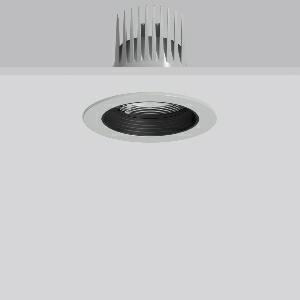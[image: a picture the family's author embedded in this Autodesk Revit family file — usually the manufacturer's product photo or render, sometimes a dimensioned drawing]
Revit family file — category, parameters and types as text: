
# Revit family: heledon_maxi_e_901782_004_777c
name_source: partatom
category: Lighting Fixtures
units: mm (PartAtom-declared; Revit-internal decimal feet)

## family parameters
Cut with Voids When Loaded = No
Host = Face
Light Source = No
Part Type = Normal
Room Calculation Point = No
Round Connector Dimension = Use Diameter
Shared = No

## types (1)
- HELEDON maxi E (1 x LED Modul 920 meat+, 1850 lm, 2000)
    Apparent Load = 33 VA
    Approval mark = CE
    CIE Flux Codes = 96 99 100 100 100
    Color Rendering = 90
    Color Temperature = 2000
    Default Elevation = 1800 mm
    Description = Series: HELEDON maxi
Round recessed downlight. Housing: die-cast aluminium, powder-coated. Black plastic ring and recessed LED to prevent glare from the side. Optical assembly with lens made of plastic (polycarbonate) for the best homogeneous light distribution - can be changed without tools. Special LED for illumination of meat included. Suitable for Recessed ceiling mounting. Installation without tools thanks to spring fastening system. Including separate LED converter with connecting cable 600 mm.High quality converter without flickering and stroboscopic effect. Through-wiring box (5 pole) available as accessory. The following accessories can be mounted without use of tools: interchangeable lenses, decorative glasses, honeycomb louvre, clear and frosted diffusers, white interchangeable plastic ring. 
Colour: silver
Diameter: 162 mm
Height: 3 mm
Cut-out diameter: 152 mm
Recess height: 200 mm
Luminaire: recess height: 135 mm
Lamp: LED
Socket: without socket
Colour temperature: meat +
System power: 33 W
Rated luminous flux: 1850 lm
Luminous efficiency: 56 lm/W
Control gear: Regulated power supply
Protection class: II
Type of protection: IP 20
    Height = 0 mm  [stored 0 ft]
    Lamp = 1 x LED Modul 920 meat+
    Lamp Light Flux = 1850 lm
    Lamp count = 1
    Length = 162 mm
    Lifetime = 50000 h
    Luminous efficacy = 56 lm/W
    Manufacturer = RZB
    ModVariant = No
    Model = 901782.004
    Mounting Place = Ceiling
    Mounting Type = Recessed
    Number of Poles = 1
    OnlyDefault = Yes
    Power Factor = 1
    Product Name = HELEDON maxi E
    Product group = Recessed downlights
    ProductGroupID = 402
    Protection Class = Protection class II
    Protection Degree = IP 20
    RLX_Detail_Level = 1
    RLX_Emergency_Light_Flux = 0 lm
    RLX_Emergency_Type = 0
    RLX_Emergency_Type_DB = No
    RlxData = <blob elided: 119197 chars, md5=445ec9c8>
    Socket = socket
    Standby Power = 0 W
    System Light Flux = 1850 lm
    System Power = 33 W
    Type Comments = Product without accessories
    Type Image = 901663.004.jpg
    URL = http://relux.com
    VarID = ---
    Voltage = 230 V
    Voltage Range = 220-240 V
    Weight = 0.00 kg
    Width = 0 mm  [stored 0 ft]

note: [stored X ft] marks values corroborated as IEEE doubles in the binary element streams (Revit-internal decimal feet)

## geometry (parser evidence)
native form markers: Blend x4, Sweep x12
no freeform markers — native parametric forms only
